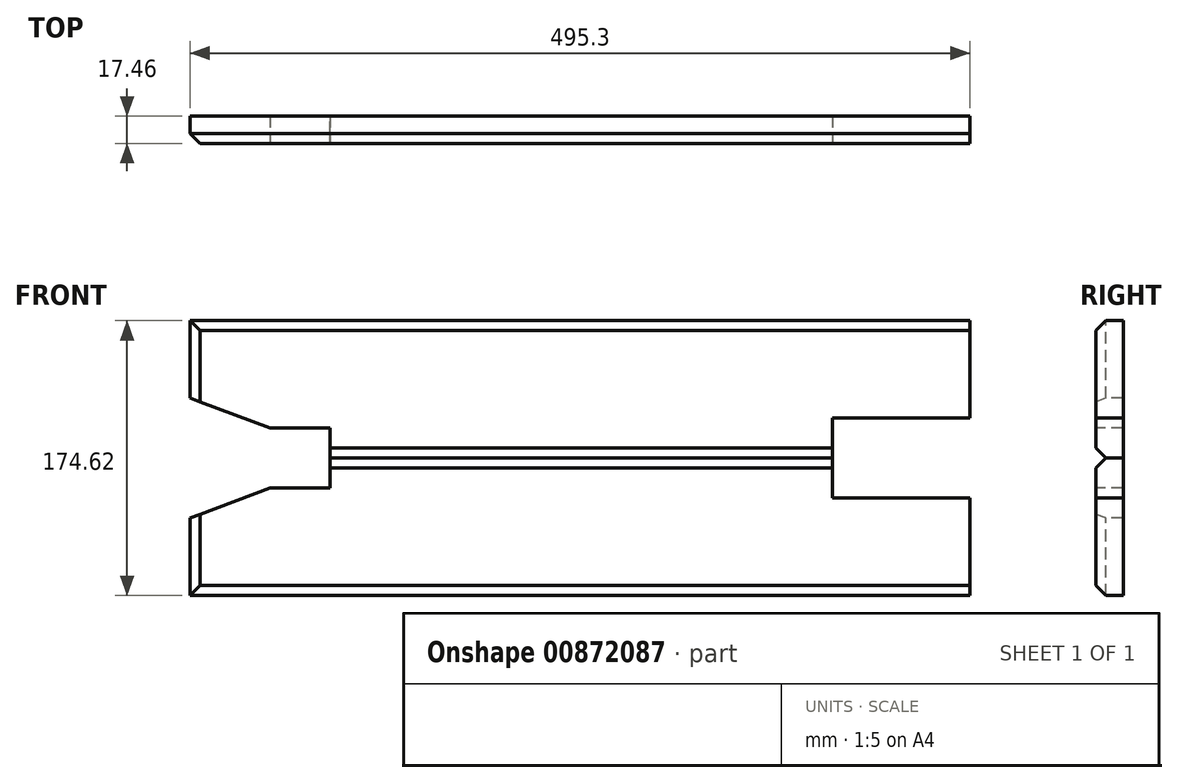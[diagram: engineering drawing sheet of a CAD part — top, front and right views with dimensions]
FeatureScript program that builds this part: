
annotation { "Feature Type Name" : "Feature", "Feature Type Description" : "" }
export const myFeature = defineFeature(function(context is Context, id is Id, definition is map)
    precondition{}
    {
        {
            var Q0;
            Q0=qCreatedBy(makeId("Front.planeOp"),FACE);
            var sketch = newSketch(context, id + "F0", { "sketchPlane" : qUnion([Q0])});
            skLineSegment(sketch, "E0.bottom", {"start": v(0, 0) * mm, "end": v(495.3, 0) * mm});
            skLineSegment(sketch, "E0.top", {"start": v(0, 87.31) * mm, "end": v(495.3, 87.31) * mm});
            skLineSegment(sketch, "E0.left", {"start": v(0, 0) * mm, "end": v(0, 87.31) * mm});
            skLineSegment(sketch, "E0.right", {"start": v(495.3, 0) * mm, "end": v(495.3, 87.31) * mm});
            skSolve(sketch);
        }
        {
            var Q0;
            Q0=qSketchRegion(id+"F0",true);
            extrude(context, id + "F1", {"entities" : qUnion([Q0]), "depth" : 17.46 * mm});
        }
        {
            var Q0;
            Q0=makeQuery(id+"F1.opExtrude","SWEPT_FACE",FACE,{"disambiguationData":[OSD([sQuery(id+"F0.wireOp",EDGE,"E0.bottom")])]});
            var sketch = newSketch(context, id + "F2", { "sketchPlane" : qUnion([Q0])});
            skLineSegment(sketch, "E1.bottom", {"start": v(0, 0) * mm, "end": v(495.3, 0) * mm});
            skLineSegment(sketch, "E1.top", {"start": v(0, 17.46) * mm, "end": v(495.3, 17.46) * mm});
            skLineSegment(sketch, "E1.left", {"start": v(0, 0) * mm, "end": v(0, 17.46) * mm});
            skLineSegment(sketch, "E1.right", {"start": v(495.3, 0) * mm, "end": v(495.3, 17.46) * mm});
            skSolve(sketch);
        }
        {
            var Q0;
            Q0=qSketchRegion(id+"F2",true);
            extrude(context, id + "F3", {"entities" : qUnion([Q0]), "depth" : 87.31 * mm});
        }
        {
            var Q0;
            Q0=makeQuery(id+"F3.opExtrude","SWEPT_FACE",FACE,{"disambiguationData":[OSD([sQuery(id+"F2.wireOp",EDGE,"E1.top")])]});
            var sketch = newSketch(context, id + "F4", { "sketchPlane" : qUnion([Q0])});
            skLineSegment(sketch, "E2", {"start": v(495.3, 0) * mm, "end": v(495.3, -25.4) * mm});
            skLineSegment(sketch, "E3", {"start": v(495.3, -25.4) * mm, "end": v(407.99, -25.4) * mm});
            skLineSegment(sketch, "E4", {"start": v(407.99, -25.4) * mm, "end": v(407.99, 0) * mm});
            skLineSegment(sketch, "E5", {"start": v(407.99, 0) * mm, "end": v(407.99, 25.4) * mm});
            skLineSegment(sketch, "E6", {"start": v(407.99, 25.4) * mm, "end": v(495.3, 25.4) * mm});
            skLineSegment(sketch, "E7", {"start": v(495.3, 25.4) * mm, "end": v(495.3, 0) * mm});
            skLineSegment(sketch, "E8", {"start": v(0, 38.1) * mm, "end": v(50.8, 19.05) * mm});
            skLineSegment(sketch, "E9", {"start": v(50.8, -19.05) * mm, "end": v(0, -38.1) * mm});
            skLineSegment(sketch, "E10", {"start": v(0, -38.1) * mm, "end": v(0, 0) * mm});
            skLineSegment(sketch, "E11", {"start": v(0, 0) * mm, "end": v(0, 38.1) * mm});
            skLineSegment(sketch, "E12", {"start": v(50.8, 19.05) * mm, "end": v(88.9, 19.05) * mm});
            skLineSegment(sketch, "E13", {"start": v(88.9, 19.05) * mm, "end": v(88.9, 0) * mm});
            skLineSegment(sketch, "E14", {"start": v(88.9, 0) * mm, "end": v(88.9, -19.05) * mm});
            skLineSegment(sketch, "E15", {"start": v(88.9, -19.05) * mm, "end": v(50.8, -19.05) * mm});
            skLineSegment(sketch, "E16", {"start": v(0, 0) * mm, "end": v(88.9, 0) * mm});
            skSolve(sketch);
        }
        {
            var Q0;
            Q0=qSketchRegion(id+"F4",true);
            extrude(context, id + "F5", {"entities" : qUnion([Q0]), "operationType" : NewBodyOperationType.REMOVE, "oppositeDirection" : true, "depth" : 25.4 * mm});
        }
        {
            var Q0;
            Q0=makeQuery(id+"F1.opExtrude","CAP_EDGE",EDGE,{"disambiguationData":[OSD([sQuery(id+"F0.wireOp",EDGE,"E0.top")])],"isStart":false});
            var Q1;
            Q1=makeQuery(id+"F3.opExtrude","CAP_EDGE",EDGE,{"disambiguationData":[OSD([sQuery(id+"F2.wireOp",EDGE,"E1.top")])],"isStart":false});
            var Q2;
            Q2=makeQuery(id+"F3.opExtrude","CAP_EDGE",EDGE,{"disambiguationData":[OSD([sQuery(id+"F2.wireOp",EDGE,"E1.top")])],"isStart":true});
            var Q3;
            Q3=makeQuery(id+"F1.opExtrude","CAP_EDGE",EDGE,{"disambiguationData":[OSD([sQuery(id+"F0.wireOp",EDGE,"E0.left")])],"isStart":false});
            var Q4;
            Q4=makeQuery(id+"F3.opExtrude","SWEPT_EDGE",EDGE,{"disambiguationData":[OSD([sQuery(id+"F2.wireOp",EDGE,"E1.top"),sQuery(id+"F2.wireOp",EDGE,"E1.left")])]});
            chamfer(context, id + "F6", {"entities" : qUnion([Q0, Q1, Q2, Q3, Q4]), "width" : 6.35 * mm, "tangentPropagation" : true});
        }
        {
            var Q0;
            Q0=makeQuery(id+"F1.opExtrude","CAP_EDGE",EDGE,{"disambiguationData":[OSD([sQuery(id+"F0.wireOp",EDGE,"E0.bottom")])],"isStart":false});
            chamfer(context, id + "F7", {"entities" : qUnion([Q0]), "width" : 6.35 * mm, "tangentPropagation" : true});
        }
    });
